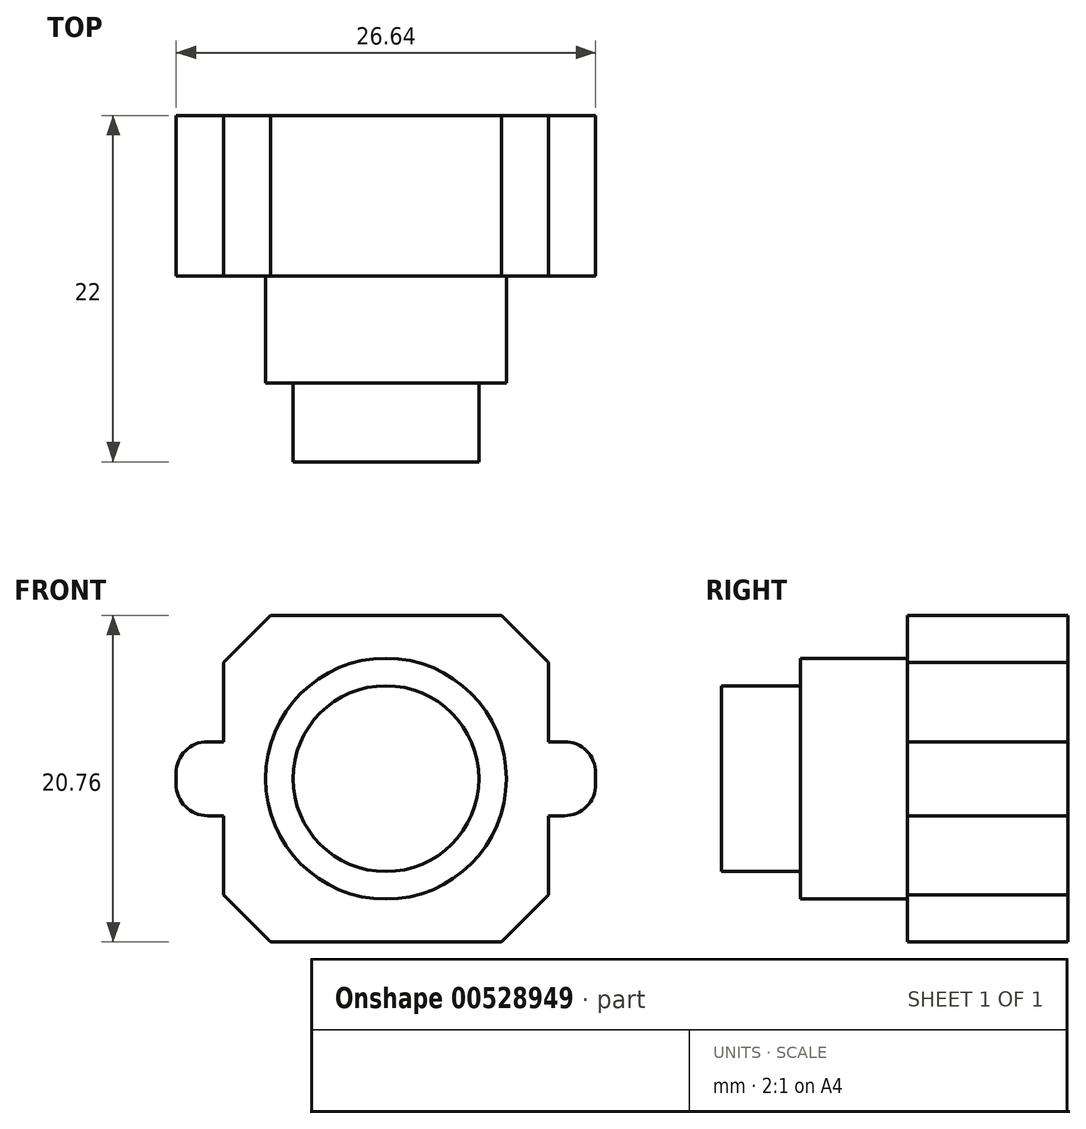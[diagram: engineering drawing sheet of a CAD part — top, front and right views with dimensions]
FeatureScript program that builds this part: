
annotation { "Feature Type Name" : "Feature", "Feature Type Description" : "" }
export const myFeature = defineFeature(function(context is Context, id is Id, definition is map)
    precondition{}
    {
        {
            var Q0;
            Q0=qCreatedBy(makeId("Front.planeOp"),FACE);
            var sketch = newSketch(context, id + "F0", { "sketchPlane" : qUnion([Q0])});
            skLineSegment(sketch, "E0.bottom", {"start": v(10.32, 10.38) * mm, "end": v(-10.33, 10.38) * mm});
            skLineSegment(sketch, "E0.top", {"start": v(10.33, -10.38) * mm, "end": v(-10.32, -10.38) * mm});
            skLineSegment(sketch, "E0.left", {"start": v(10.33, 10.38) * mm, "end": v(10.33, 2.35) * mm});
            skLineSegment(sketch, "E0.right", {"start": v(-10.32, 10.38) * mm, "end": v(-10.32, 2.35) * mm});
            skPoint(sketch, "E0.middle", {"position": v(0, 0) * mm});
            skLineSegment(sketch, "E1", {"start": v(-10.32, 0) * mm, "end": v(10.33, 0) * mm, "construction": true});
            skLineSegment(sketch, "E2.bottom", {"start": v(13.33, 2.35) * mm, "end": v(10.33, 2.35) * mm});
            skLineSegment(sketch, "E2.top", {"start": v(13.33, -2.35) * mm, "end": v(10.33, -2.35) * mm});
            skLineSegment(sketch, "E2.left", {"start": v(13.33, 2.35) * mm, "end": v(13.33, -2.35) * mm});
            skLineSegment(sketch, "E2.right", {"start": v(7.33, 2.35) * mm, "end": v(7.33, -2.35) * mm, "construction": true});
            skPoint(sketch, "E2.middle", {"position": v(10.33, 0) * mm});
            skLineSegment(sketch, "E3.bottom", {"start": v(-10.32, 2.35) * mm, "end": v(-13.32, 2.35) * mm});
            skLineSegment(sketch, "E3.top", {"start": v(-10.32, -2.35) * mm, "end": v(-13.32, -2.35) * mm});
            skLineSegment(sketch, "E3.left", {"start": v(-7.32, 2.35) * mm, "end": v(-7.32, -2.35) * mm, "construction": true});
            skLineSegment(sketch, "E3.right", {"start": v(-13.32, 2.35) * mm, "end": v(-13.32, -2.35) * mm});
            skPoint(sketch, "E3.middle", {"position": v(-10.32, 0) * mm});
            skLineSegment(sketch, "E4.trimOffspring", {"start": v(10.33, -2.35) * mm, "end": v(10.33, -10.38) * mm});
            skLineSegment(sketch, "E5.trimOffspring", {"start": v(-10.32, -2.35) * mm, "end": v(-10.32, -10.38) * mm});
            skSolve(sketch);
        }
        {
            var Q0;
            Q0=makeQuery(id+"F0.imprint","IMPRINT",FACE,{"disambiguationData":[TD([[makeQuery(id+"F0.imprint","IMPRINT",EDGE,{"derivedFrom":sQuery(id+"F0.wireOp",EDGE,"E0.bottom")}),1.0]])]});
            extrude(context, id + "F1", {"entities" : qUnion([Q0]), "depth" : 10.2 * mm, "offsetDistance" : 25 * mm});
        }
        {
            var Q0;
            Q0=makeQuery(id+"F1.opExtrude","SWEPT_EDGE",EDGE,{"disambiguationData":[OSD([sQuery(id+"F0.wireOp",EDGE,"E3.top"),sQuery(id+"F0.wireOp",EDGE,"E3.right")])]});
            var Q1;
            Q1=makeQuery(id+"F1.opExtrude","SWEPT_EDGE",EDGE,{"disambiguationData":[OSD([sQuery(id+"F0.wireOp",EDGE,"E3.bottom"),sQuery(id+"F0.wireOp",EDGE,"E3.right")])]});
            var Q2;
            Q2=makeQuery(id+"F1.opExtrude","SWEPT_EDGE",EDGE,{"disambiguationData":[OSD([sQuery(id+"F0.wireOp",EDGE,"E2.top"),sQuery(id+"F0.wireOp",EDGE,"E2.left")])]});
            var Q3;
            Q3=makeQuery(id+"F1.opExtrude","SWEPT_EDGE",EDGE,{"disambiguationData":[OSD([sQuery(id+"F0.wireOp",EDGE,"E2.bottom"),sQuery(id+"F0.wireOp",EDGE,"E2.left")])]});
            fillet(context, id + "F2", {"entities" : qUnion([Q0, Q1, Q2, Q3]), "radius" : 2 * mm, "tangentPropagation" : true, "allowEdgeOverflow" : false});
        }
        {
            var Q0;
            Q0=makeQuery(id+"F1.opExtrude","CAP_FACE",FACE,{"disambiguationData":[OSD([sQuery(id+"F0.wireOp",EDGE,"E0.bottom"),sQuery(id+"F0.wireOp",EDGE,"E0.top"),sQuery(id+"F0.wireOp",EDGE,"E0.left"),sQuery(id+"F0.wireOp",EDGE,"E0.right"),sQuery(id+"F0.wireOp",EDGE,"E2.bottom"),sQuery(id+"F0.wireOp",EDGE,"E2.top"),sQuery(id+"F0.wireOp",EDGE,"E2.left"),sQuery(id+"F0.wireOp",EDGE,"E3.bottom"),sQuery(id+"F0.wireOp",EDGE,"E3.top"),sQuery(id+"F0.wireOp",EDGE,"E3.right"),sQuery(id+"F0.wireOp",EDGE,"E4.trimOffspring"),sQuery(id+"F0.wireOp",EDGE,"E5.trimOffspring")])],"isStart":false});
            var sketch = newSketch(context, id + "F3", { "sketchPlane" : qUnion([Q0])});
            skCircle(sketch, "E6", {"center": v(0, 0) * mm, "radius": 7.65 * mm});
            skSolve(sketch);
        }
        {
            var Q0;
            Q0=makeQuery(id+"F3.imprint","IMPRINT",FACE,{"disambiguationData":[TD([[makeQuery(id+"F3.imprint","IMPRINT",EDGE,{"derivedFrom":sQuery(id+"F3.wireOp",EDGE,"E6")}),1.0]])]});
            extrude(context, id + "F4", {"entities" : qUnion([Q0]), "operationType" : NewBodyOperationType.ADD, "depth" : 6.8 * mm, "offsetDistance" : 25 * mm});
        }
        {
            var Q0;
            Q0=makeQuery(id+"F1.opExtrude","SWEPT_EDGE",EDGE,{"disambiguationData":[OSD([sQuery(id+"F0.wireOp",EDGE,"E0.top"),sQuery(id+"F0.wireOp",EDGE,"E5.trimOffspring")])]});
            var Q1;
            Q1=makeQuery(id+"F1.opExtrude","SWEPT_EDGE",EDGE,{"disambiguationData":[OSD([sQuery(id+"F0.wireOp",EDGE,"E0.bottom"),sQuery(id+"F0.wireOp",EDGE,"E0.right")])]});
            var Q2;
            Q2=makeQuery(id+"F1.opExtrude","SWEPT_EDGE",EDGE,{"disambiguationData":[OSD([sQuery(id+"F0.wireOp",EDGE,"E0.top"),sQuery(id+"F0.wireOp",EDGE,"E4.trimOffspring")])]});
            var Q3;
            Q3=makeQuery(id+"F1.opExtrude","SWEPT_EDGE",EDGE,{"disambiguationData":[OSD([sQuery(id+"F0.wireOp",EDGE,"E0.bottom"),sQuery(id+"F0.wireOp",EDGE,"E0.left")])]});
            chamfer(context, id + "F5", {"entities" : qUnion([Q0, Q1, Q2, Q3]), "width" : 3 * mm, "tangentPropagation" : true});
        }
        {
            var Q0;
            Q0=makeQuery(id+"F4.opExtrude","CAP_FACE",FACE,{"disambiguationData":[OSD([sQuery(id+"F3.wireOp",EDGE,"E6")])],"isStart":false});
            var sketch = newSketch(context, id + "F6", { "sketchPlane" : qUnion([Q0])});
            skCircle(sketch, "E7", {"center": v(0, 0) * mm, "radius": 5.9 * mm});
            skSolve(sketch);
        }
        {
            var Q0;
            Q0 = qSketchRegion(id + "F6", true);
            extrude(context, id + "F7", {"entities" : qUnion([Q0]), "operationType" : NewBodyOperationType.ADD, "depth" : 5 * mm, "offsetDistance" : 25 * mm});
        }
    });
